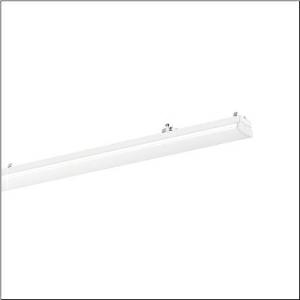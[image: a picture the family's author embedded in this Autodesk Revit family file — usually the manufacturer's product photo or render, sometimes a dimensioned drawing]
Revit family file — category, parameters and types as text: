
# Revit family: licross_r__21_recessed_opal_mo_52tl1ddn445g_2a2a
name_source: partatom
category: Lighting Fixtures
units: mm (PartAtom-declared; Revit-internal decimal feet)

## family parameters
Cut with Voids When Loaded = No
Host = Face
Light Source = No
Part Type = Normal
Room Calculation Point = No
Round Connector Dimension = Use Diameter
Shared = No

## types (1)
- --- (1 x LED, 4500 lm, 25.8 W, 4000K)
    Apparent Load = 26 VA
    CIE Flux Codes = 44 73 91 87 100
    Color Rendering = 80
    Color Temperature = 4000K
    Default Elevation = 1800 mm
    Description = Licross® 21 recessed opal MO, luminaire insert, of sheet steel, galvanised, coil coated, white, length: 1.500mm, width: 66mm, height: 67mm, LED rated luminous flux: 4.500lm, light colour: 840, control gear: DALI 2, with plug, 5-pole, with phase selection, mains connection: 220..240V, AC, 50/60Hz, rated input power: 26W, internal wiring halogen-free, primary optical cover: cover, of PMMA, light emission: direct with ceiling illumination distribution, primary light characteristic: symmetric, protection rating (complete): IP40, insulation class (complete): insulation class I (protective earthing), certification: CE, ENEC, VDE, UKCA, protection symbol: D if used in an environment without relevant dust loads with corresponding accessories, impact resistance: IK06, permissible ambient temperature for indoor applications: -25..+45°C, corresponds to IFS (International Featured Standards) requirements for safety and quality in the food industry, reducing of maximum allowable ambient temperature of 5°C with ceiling mounting, LABS conformity tested according to VDMA 24364:2018-05, packaging unit: 1 piece
    Height = 83 mm
    Lamp = 1 x LED
    Lamp Light Flux = 4500 lm
    Lamp Power = 25.8 W
    Lamp count = 1
    Length = 1500 mm
    Luminous efficacy = 174 lm/W
    Manufacturer = Siteco
    ModVariant = No
    Model = 52TL1DDN445G
    Mounting Place = Ceiling
    Mounting Type = Pendant
    Number of Poles = 1
    OnlyDefault = Yes
    Power Factor = 1
    Product Name = Licross® 21 recessed opal MO
    Product group = luminaire insert | ceiling pendant
    ProductGroupID = 902
    Protection Class = Protection class I
    Protection Degree = IP 40
    RLX_Detail_Level = 1
    RLX_Emergency_Light_Flux = 0 lm
    RLX_Emergency_Type = 0
    RLX_Emergency_Type_DB = No
    RlxData = <blob elided: 26453 chars, md5=a3815691>
    Socket = socket
    Standby Power = 0 W
    System Light Flux = 4500 lm
    System Power = 26 W
    Type Comments = factory setting: luminous flux: 100 % | dim-lin: 254 | 172 mA
    Type Image = l_1313666.jpg
    URL = http://relux.com
    VarID = @adj_084525
    Voltage = 0 V
    Weight = 0.00 kg
    Width = 76 mm

## geometry (parser evidence)
native form markers: Blend x4, Sweep x11
no freeform markers — native parametric forms only
